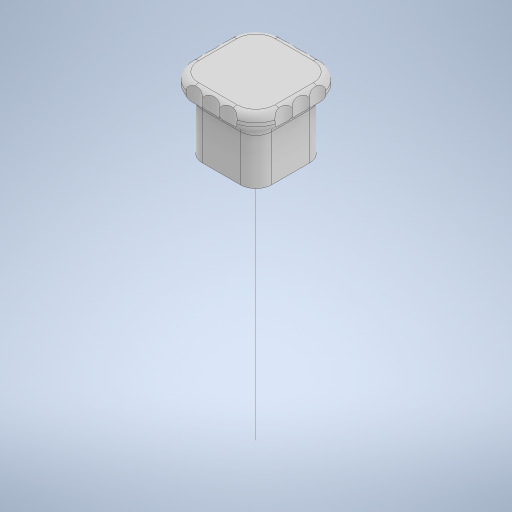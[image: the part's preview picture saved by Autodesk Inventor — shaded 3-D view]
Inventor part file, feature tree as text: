
AUTODESK INVENTOR PART (.ipt)
format: ipt  version: 2023 (Build 270158030, 158C)  size: 915,456 bytes
history: native  units: mm
features: sketch x8, extrude x7, fillet x4, other x3, projected_geometry x3, plane x2, revolve x1
ambient origin geometry x8: Origin, YZ Plane, XZ Plane, XY Plane, X Axis, Y Axis, Z Axis, Center Point
bodies: Body1 (feature_tree), Body2 (feature_tree)
feature tree (28):
  other  "body-tube"
  extrude  "Extrusion1"  Depth=2.5mm
  extrude  "Extrusion2"  Depth=2.0mm
  extrude  "Extrusion3"  Depth=4.5mm
  plane  "Work Plane1"
  extrude  "Extrusion4"  Depth=7.75mm
  fillet  "Fillet2"  Radius=7.75mm
  fillet  "Fillet3"  Radius=2.0mm
  extrude  "Extrusion5"  Depth=16.0mm
  extrude  "Extrusion6"  Depth=2.5mm
  fillet  "Fillet4"  Radius=8.9mm
  fillet  "Fillet5"  Radius=8.9mm
  plane  "Work Plane2"
  other  "Work Axis1"
  revolve  "Revolution1"  [1 undecoded]
  extrude  "Extrusion7"  Depth=3.0mm
  sketch  "Sketch1"  dims[d0=15.5mm d1=15.5mm d2=2.5mm]
  sketch  "Sketch2"  dims[d3=2.0mm d4=2.0mm d5=2.0mm]
  sketch  "Sketch3"  dims[d6=2.0mm d7=4.5mm]
  projected_geometry  "Projected Loop1"
  sketch  "Sketch4"  dims[d8=4.5mm d9=7.75mm d10=7.75mm d11=16.3mm d12=2.0mm]
  sketch  "Sketch5"  dims[d13=16.0mm d14=16.0mm]
  projected_geometry  "Projected Loop2"
  other  "lid"
  sketch  "Sketch6"  dims[d17=2.5mm d18=2.5mm d19=8.9mm d20=8.9mm]
  projected_geometry  "Projected Loop3"
  sketch  "Sketch8"  dims[d21=2.0mm d22=73.0mm d23=0.0mm]
  sketch  "Sketch9"  dims[d24=3.0mm d25=0.0mm d26=1.0mm d27=1.0mm d28=1.0mm d29=1.0mm d30=3.5mm d31=3.5mm d32=15.0mm d33=0.0mm d34=0.0mm d35=65.0mm d36=0.0mm d37=1.570796mm d39=2.0mm d40=5.0mm d41=15.5mm d42=0.0mm d43=5.0mm d44=0.0mm d45=2.0mm d46=2.5mm d47=6.0mm d48=6.0mm d49=6.0mm d50=6.0mm d51=6.0mm d52=5.0mm d53=3.0mm d54=360.0deg d55=5.0mm d56=5.0mm d57=8.0mm d61=5.0mm d62=40.0mm d64=360.0deg d66=0.0mm d67=-0.174533mm d68=8.0mm d69=8.0mm d70=8.9mm d71=8.9mm d72=6.0mm d73=5.0mm d74=5.0mm d75=3.0mm d76=3.0mm d77=3.0mm d78=3.0mm d79=7.5mm d80=4.5mm d81=7.5mm d82=6.0mm d83=6.0mm d84=6.0mm]
note: 1 required parameter value undecoded (feature->parameter linkage not recoverable at this tier; creation-order binding heuristic only, values carry confidence <= 0.55)
